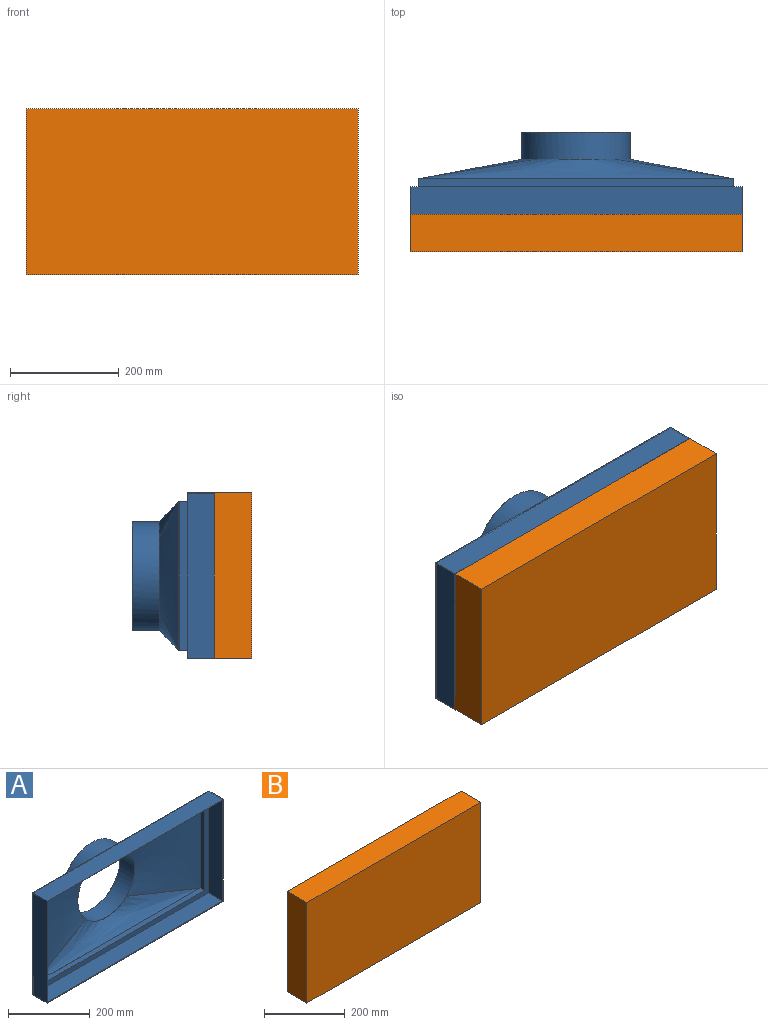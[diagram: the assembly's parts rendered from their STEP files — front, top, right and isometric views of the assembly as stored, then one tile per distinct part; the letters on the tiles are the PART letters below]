
ASSEMBLY  parts=2 mates=1
PART A: 30 faces, bbox 613x154x308 mm
  f0: plane 610x305mm, normal (0,1,0), area 26550mm2, adj f1,f2,f3,f4,f6,f7,f8,f9
  f1: plane 305x50mm, normal (1,0,0), area 15250mm2, adj f0,f2,f4,f5
  f2: plane 610x50mm, normal (0,0,-1), area 30500mm2, adj f0,f1,f3,f5
  f3: plane 305x50mm, normal (-1,0,0), area 15250mm2, adj f0,f2,f4,f5
  f4: plane 610x50mm, normal (0,0,1), area 30500mm2, adj f0,f1,f3,f5
  f5: plane 610x305mm, normal (0,-1,0), area 2736mm2, adj f1,f2,f3,f4,f17,f18,f19,f20
  f6: plane 580x15mm, normal (0,0,1), area 8700mm2, adj f0,f7,f9,f13
  f7: plane 275x15mm, normal (1,0,0), area 4125mm2, adj f0,f6,f8,f12
  f8: plane 580x15mm, normal (0,0,-1), area 8700mm2, adj f0,f7,f9,f15
  f9: plane 275x15mm, normal (-1,0,0), area 4125mm2, adj f0,f6,f8,f14
  f10: cylinder r=100mm len=200mm, axis (0,1,0), area 31415.9mm2, adj f11,f12,f13,f14,f15
  f11: plane 200x200mm, normal (0,1,0), area 935.4mm2, adj f10,f25
  f12: bspline ~277.75x220.4mm, area 43485mm2, adj f7,f10,f13,f15
  f13: bspline ~585.8x69.17mm, area 25259.3mm2, adj f6,f10,f12,f14
  f14: bspline ~277.75x220.4mm, area 43485mm2, adj f9,f10,f13,f15
  f15: bspline ~585.8x69.17mm, area 25259.3mm2, adj f8,f10,f12,f14
  f16: plane 607x302mm, normal (0,-1,0), area 26370mm2, adj f17,f18,f19,f20,f21,f22,f23,f24
  f17: plane 302x48.5mm, normal (-1,0,0), area 14647mm2, adj f5,f16,f18,f20
  f18: plane 607x48.5mm, normal (0,0,1), area 29439.5mm2, adj f5,f16,f17,f19
  f19: plane 302x48.5mm, normal (1,0,0), area 14647mm2, adj f5,f16,f18,f20
  f20: plane 607x48.5mm, normal (0,0,-1), area 29439.5mm2, adj f5,f16,f17,f19
  f21: plane 577.11x15.97mm, normal (0,0,-1), area 9093.9mm2, adj f16,f22,f24,f26,f27,f28
  f22: plane 272.26x15.52mm, normal (-1,0,0), area 4147mm2, adj f16,f21,f23,f26
  f23: plane 577.11x15.97mm, normal (0,0,1), area 9093.9mm2, adj f16,f22,f24,f26,f28,f29
  f24: plane 272.26x15.52mm, normal (1,0,0), area 4147mm2, adj f16,f21,f23,f28
  f25: cylinder r=98.5mm len=197mm, axis (0,1,0), area 31631.6mm2, adj f11,f26,f27,f28,f29
  f26: offset ~283.5x226.14mm, area 43241.2mm2, adj f21,f22,f23,f25,f27,f29
  f27: offset ~594.6x72.17mm, area 24601.8mm2, adj f21,f25,f26,f28
  f28: offset ~283.5x226.14mm, area 43241.2mm2, adj f21,f23,f24,f25,f27,f29
  f29: offset ~594.6x72.17mm, area 24601.8mm2, adj f23,f25,f26,f28
PART B: 6 faces, bbox 610x69x305 mm
  f0: plane 610x69mm, normal (0,0,-1), area 42090mm2, adj f1,f3,f4,f5
  f1: plane 305x69mm, normal (1,0,0), area 21045mm2, adj f0,f2,f4,f5
  f2: plane 610x69mm, normal (0,0,1), area 42090mm2, adj f1,f3,f4,f5
  f3: plane 305x69mm, normal (-1,0,0), area 21045mm2, adj f0,f2,f4,f5
  f4: plane 610x305mm, normal (0,1,0), area 186050mm2, adj f0,f1,f2,f3
  f5: plane 610x305mm, normal (0,-1,0), area 186050mm2, adj f0,f1,f2,f3
PLACE A at identity
PLACE B at identity fixed
MATE fastened A.f5 <-> B.f4  axis (0,-1,0) through (305,-31,152.5)mm
